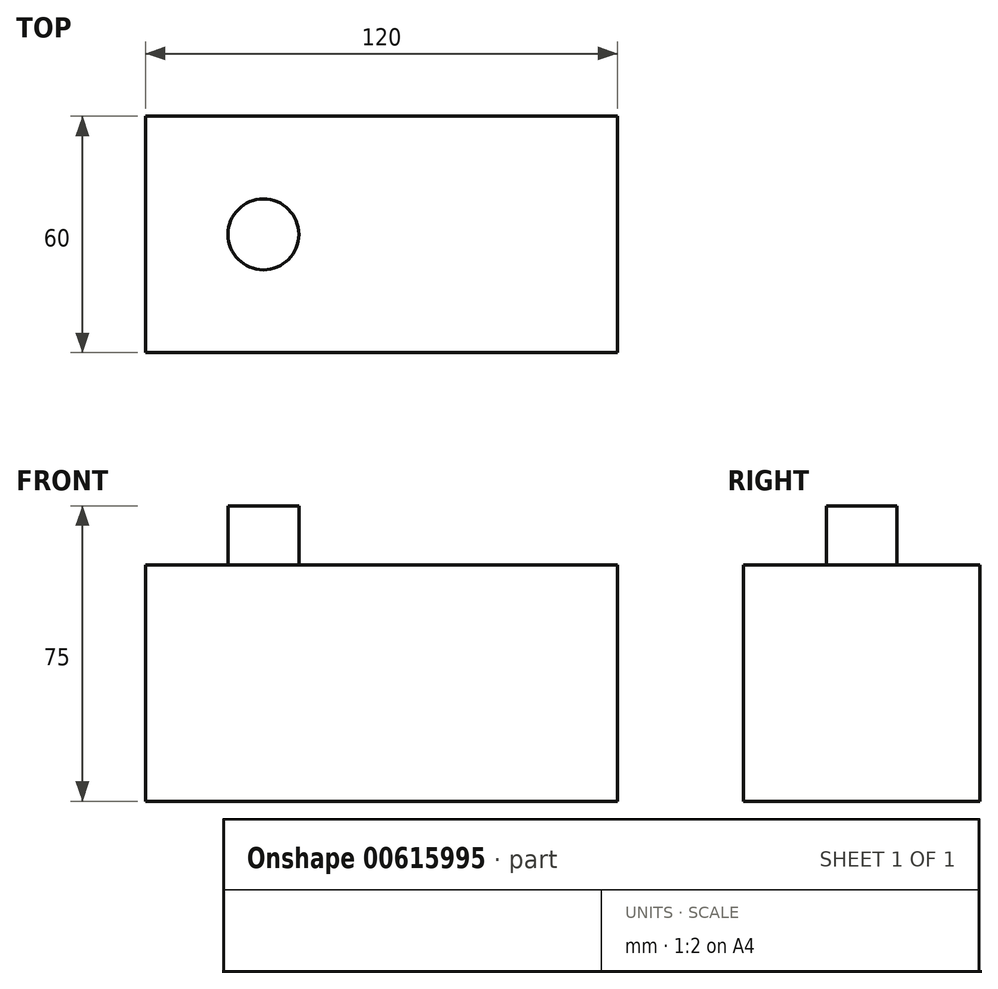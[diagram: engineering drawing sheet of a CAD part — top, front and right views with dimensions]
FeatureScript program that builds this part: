
annotation { "Feature Type Name" : "Feature", "Feature Type Description" : "" }
export const myFeature = defineFeature(function(context is Context, id is Id, definition is map)
    precondition{}
    {
        {
            var Q0;
            Q0=qCreatedBy(makeId("Front.planeOp"),FACE);
            var sketch = newSketch(context, id + "F0", { "sketchPlane" : qUnion([Q0])});
            skLineSegment(sketch, "E0.bottom", {"start": v(0, 0) * mm, "end": v(120, 0) * mm});
            skLineSegment(sketch, "E0.top", {"start": v(0, 60) * mm, "end": v(120, 60) * mm});
            skLineSegment(sketch, "E0.left", {"start": v(0, 0) * mm, "end": v(0, 60) * mm});
            skLineSegment(sketch, "E0.right", {"start": v(120, 0) * mm, "end": v(120, 60) * mm});
            skSolve(sketch);
        }
        {
            var Q0;
            Q0=makeQuery(id+"F0.imprint","IMPRINT",FACE,{"disambiguationData":[TD([[makeQuery(id+"F0.imprint","IMPRINT",EDGE,{"derivedFrom":sQuery(id+"F0.wireOp",EDGE,"E0.bottom")}),1.0]])]});
            extrude(context, id + "F1", {"entities" : qUnion([Q0]), "endBound" : BoundingType.SYMMETRIC, "depth" : 60 * mm, "offsetDistance" : 25 * mm});
        }
        {
            var Q0;
            Q0=makeQuery(id+"F1.opExtrude","SWEPT_FACE",FACE,{"disambiguationData":[OSD([sQuery(id+"F0.wireOp",EDGE,"E0.top")])]});
            var sketch = newSketch(context, id + "F2", { "sketchPlane" : qUnion([Q0])});
            skLineSegment(sketch, "E1", {"start": v(0, 0) * mm, "end": v(120, 0) * mm, "construction": true});
            skLineSegment(sketch, "E2", {"start": v(30, 30) * mm, "end": v(30, -30) * mm, "construction": true});
            skLineSegment(sketch, "E3", {"start": v(60, 30) * mm, "end": v(60, -30) * mm, "construction": true});
            skCircle(sketch, "E4", {"center": v(30, 0) * mm, "radius": 9 * mm});
            skCircle(sketch, "E5", {"center": v(60, 0) * mm, "radius": 9 * mm});
            skLineSegment(sketch, "E6", {"start": v(90, 30) * mm, "end": v(90, -30) * mm, "construction": true});
            skCircle(sketch, "E7", {"center": v(90, 0) * mm, "radius": 9 * mm});
            skSolve(sketch);
        }
        {
            var Q0;
            Q0=makeQuery(id+"F2.imprint","IMPRINT",FACE,{"disambiguationData":[TD([[makeQuery(id+"F2.imprint","IMPRINT",EDGE,{"derivedFrom":sQuery(id+"F2.wireOp",EDGE,"E4")}),1.0]])]});
            extrude(context, id + "F3", {"entities" : qUnion([Q0]), "operationType" : NewBodyOperationType.ADD, "depth" : 15 * mm, "offsetDistance" : 25 * mm});
        }
    });
